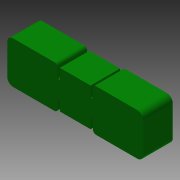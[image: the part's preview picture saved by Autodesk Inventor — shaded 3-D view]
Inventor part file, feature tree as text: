
AUTODESK INVENTOR PART (.ipt)
format: ipt  version: 2015 (Build 190159000, 159)  size: 111,616 bytes
history: native  units: in
note: dims shown in document units (in); Inventor stores cm internally (conversion verified against a paired STEP export)
features: extrude x1, sketch x1
ambient origin geometry x8: Origin, YZ Plane, XZ Plane, XY Plane, X Axis, Y Axis, Z Axis, Center Point
bodies: Solid1 (feature_tree)
feature tree (2):
  extrude  "Extrusion1"  Depth=0.5in
  sketch  "Sketch1"  dims[d0=0.32in d2=1.15in d4=0.04in d5=0.04in d10=0.05in d11=0.1in d12=0.22in d13=0.5in d14=0.0in]
